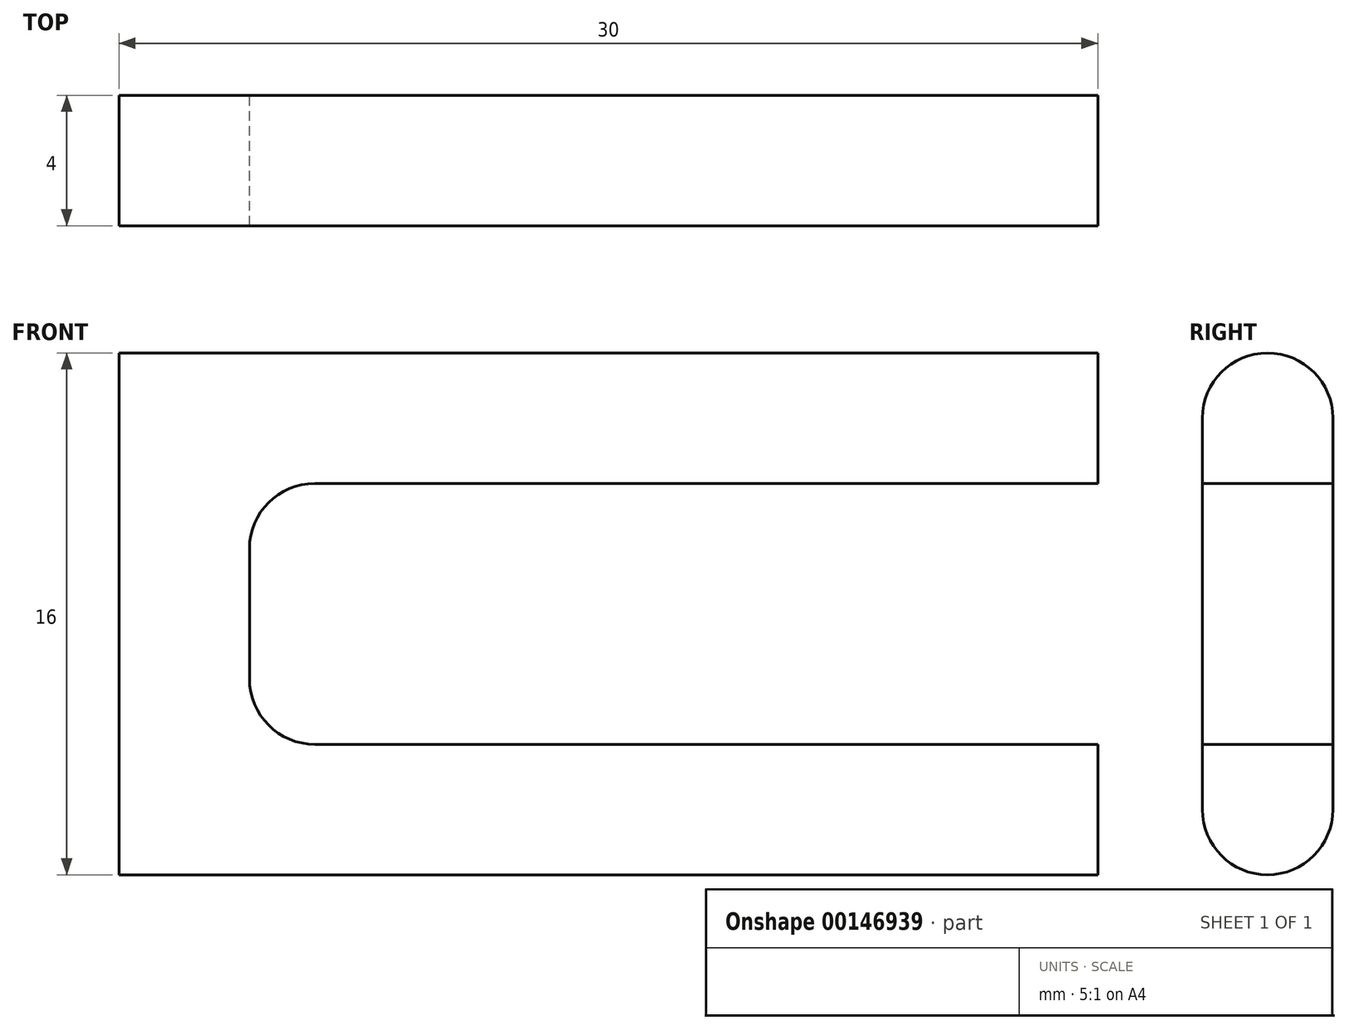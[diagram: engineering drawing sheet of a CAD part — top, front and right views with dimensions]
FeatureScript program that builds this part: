
annotation { "Feature Type Name" : "Feature", "Feature Type Description" : "" }
export const myFeature = defineFeature(function(context is Context, id is Id, definition is map)
    precondition{}
    {
        {
            var Q0;
            Q0=qCreatedBy(makeId("Front.planeOp"),FACE);
            var sketch = newSketch(context, id + "F0", { "sketchPlane" : qUnion([Q0])});
            skLineSegment(sketch, "E0", {"start": v(0, 16) * mm, "end": v(0, 12) * mm});
            skLineSegment(sketch, "E1", {"start": v(0, 12) * mm, "end": v(-26, 12) * mm});
            skLineSegment(sketch, "E2", {"start": v(-26, 12) * mm, "end": v(-26, 4) * mm});
            skLineSegment(sketch, "E3", {"start": v(-26, 4) * mm, "end": v(0, 4) * mm});
            skLineSegment(sketch, "E4", {"start": v(0, 4) * mm, "end": v(0, 0) * mm});
            skLineSegment(sketch, "E5", {"start": v(0, 0) * mm, "end": v(-30, 0) * mm});
            skLineSegment(sketch, "E6", {"start": v(-30, 0) * mm, "end": v(-30, 16) * mm});
            skLineSegment(sketch, "E7", {"start": v(-30, 16) * mm, "end": v(0, 16) * mm});
            skSolve(sketch);
        }
        {
            var Q0;
            Q0 = qSketchRegion(id + "F0", true);
            extrude(context, id + "F1", {"entities" : qUnion([Q0]), "endBound" : BoundingType.SYMMETRIC, "depth" : 4 * mm});
        }
        {
            var Q0;
            Q0=makeQuery(id+"F1.opExtrude","CAP_EDGE",EDGE,{"disambiguationData":[OSD([sQuery(id+"F0.wireOp",EDGE,"E7")])],"isStart":false});
            var Q1;
            Q1=makeQuery(id+"F1.opExtrude","CAP_EDGE",EDGE,{"disambiguationData":[OSD([sQuery(id+"F0.wireOp",EDGE,"E7")])],"isStart":true});
            var Q2;
            Q2=makeQuery(id+"F1.opExtrude","CAP_EDGE",EDGE,{"disambiguationData":[OSD([sQuery(id+"F0.wireOp",EDGE,"E5")])],"isStart":false});
            var Q3;
            Q3=makeQuery(id+"F1.opExtrude","CAP_EDGE",EDGE,{"disambiguationData":[OSD([sQuery(id+"F0.wireOp",EDGE,"E5")])],"isStart":true});
            var Q4;
            Q4=makeQuery(id+"F1.opExtrude","SWEPT_EDGE",EDGE,{"disambiguationData":[OSD([sQuery(id+"F0.wireOp",EDGE,"E2"),sQuery(id+"F0.wireOp",EDGE,"E3")])]});
            var Q5;
            Q5=makeQuery(id+"F1.opExtrude","SWEPT_EDGE",EDGE,{"disambiguationData":[OSD([sQuery(id+"F0.wireOp",EDGE,"E1"),sQuery(id+"F0.wireOp",EDGE,"E2")])]});
            fillet(context, id + "F2", {"entities" : qUnion([Q0, Q1, Q2, Q3, Q4, Q5]), "radius" : 2 * mm, "tangentPropagation" : true, "allowEdgeOverflow" : false});
        }
    });
